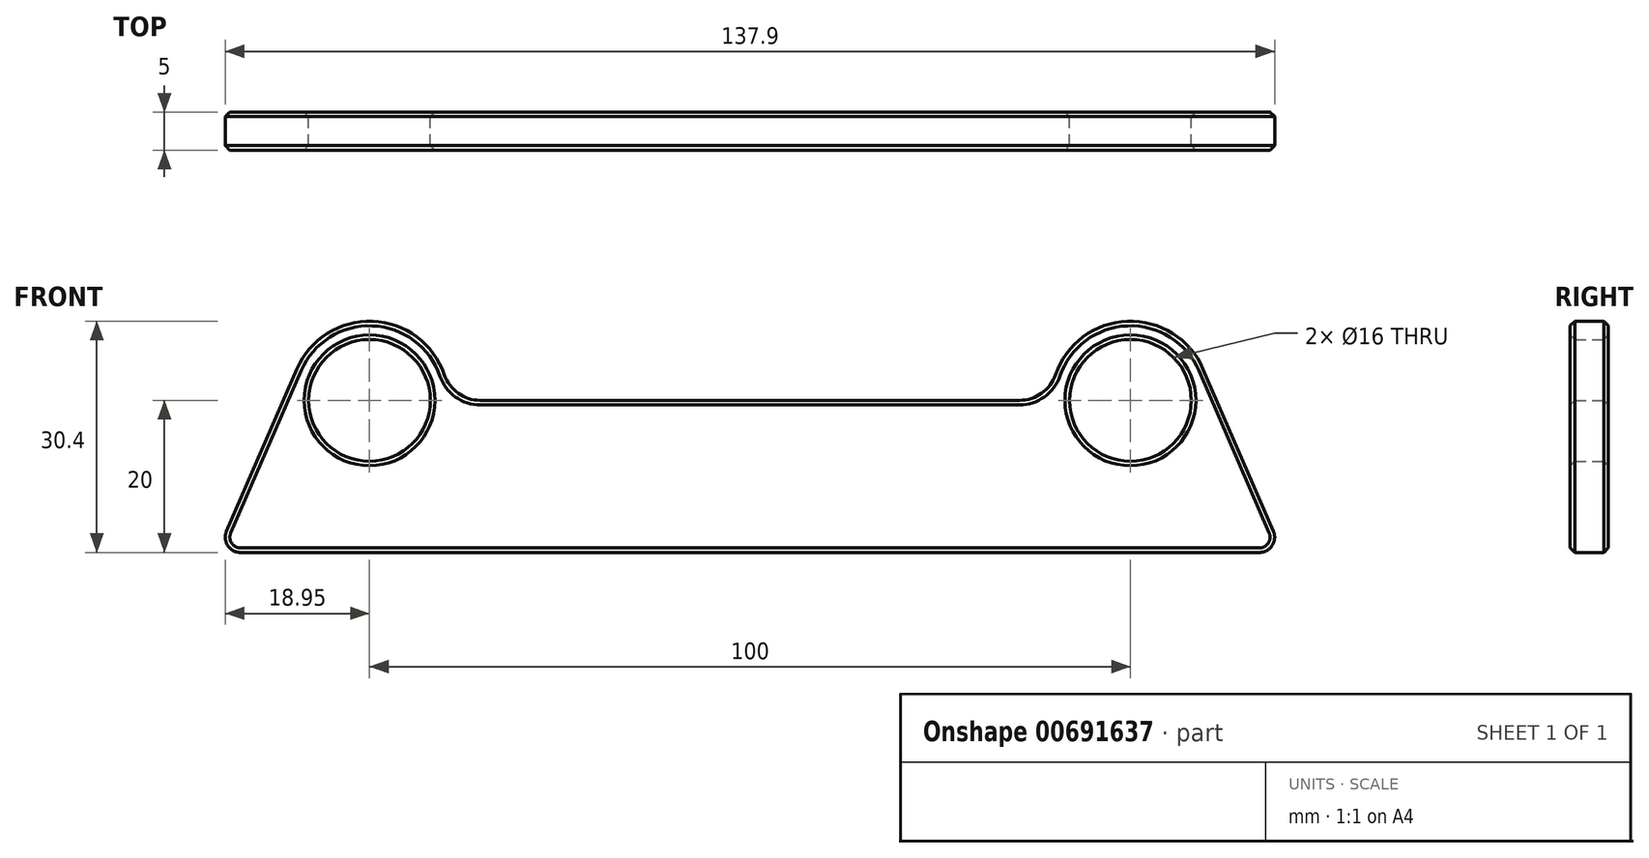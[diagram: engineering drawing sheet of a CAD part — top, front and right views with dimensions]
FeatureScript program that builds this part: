
annotation { "Feature Type Name" : "Feature", "Feature Type Description" : "" }
export const myFeature = defineFeature(function(context is Context, id is Id, definition is map)
    precondition{}
    {
        {
            var Q0;
            Q0=qCreatedBy(makeId("Front.planeOp"),FACE);
            var sketch = newSketch(context, id + "F0", { "sketchPlane" : qUnion([Q0])});
            skCircle(sketch, "E0", {"center": v(-50, 20) * mm, "radius": 2.5 * mm, "construction": true});
            skLineSegment(sketch, "E1", {"start": v(0, 0) * mm, "end": v(0, 62.59) * mm, "construction": true});
            skCircle(sketch, "E2", {"center": v(-50, 20) * mm, "radius": 8 * mm});
            skCircle(sketch, "E3.0", {"center": v(-50, 20) * mm, "radius": 10.4 * mm});
            skLineSegment(sketch, "E4", {"start": v(-70, 0) * mm, "end": v(-30, 0) * mm});
            skLineSegment(sketch, "E5", {"start": v(-50, 20) * mm, "end": v(-50, 0) * mm, "construction": true});
            skLineSegment(sketch, "E6", {"start": v(-59.54, 24.13) * mm, "end": v(-70, 0) * mm});
            skLineSegment(sketch, "E7", {"start": v(-39.6, 20) * mm, "end": v(0, 20) * mm});
            skLineSegment(sketch, "E8", {"start": v(0, 20) * mm, "end": v(0, 0) * mm});
            skLineSegment(sketch, "E9", {"start": v(-30, 0) * mm, "end": v(0, 0) * mm});
            skSolve(sketch);
        }
        {
            var Q0;
            Q0 = qSketchRegion(id + "F0", true);
            extrude(context, id + "F1", {"entities" : qUnion([Q0]), "depth" : 5 * mm, "offsetDistance" : 25 * mm});
        }
        {
            var Q0;
            Q0=makeQuery(id+"F1.opExtrude","SWEPT_EDGE",EDGE,{"disambiguationData":[OSD([sQuery(id+"F0.wireOp",EDGE,"E3.0"),sQuery(id+"F0.wireOp",EDGE,"E7")])]});
            var Q1;
            Q1=makeQuery(id+"F1.opExtrude","SWEPT_EDGE",EDGE,{"disambiguationData":[OSD([sQuery(id+"F0.wireOp",EDGE,"E3.0"),sQuery(id+"F0.wireOp",EDGE,"E6")])]});
            fillet(context, id + "F2", {"entities" : qUnion([Q0, Q1]), "radius" : 5 * mm, "tangentPropagation" : true, "allowEdgeOverflow" : false});
        }
        {
            var Q0;
            Q0=makeQuery(id+"F1.opExtrude","SWEPT_EDGE",EDGE,{"disambiguationData":[OSD([sQuery(id+"F0.wireOp",EDGE,"E4"),sQuery(id+"F0.wireOp",EDGE,"E6")])]});
            fillet(context, id + "F3", {"entities" : qUnion([Q0]), "radius" : 2 * mm, "tangentPropagation" : true, "allowEdgeOverflow" : false});
        }
        {
            var Q0;
            Q0=makeQuery(id+"F1.opExtrude","SWEPT_BODY",BODY,{"disambiguationData":[OSD([sQuery(id+"F0.wireOp",EDGE,"E2"),sQuery(id+"F0.wireOp",EDGE,"E3.0"),sQuery(id+"F0.wireOp",EDGE,"E4"),sQuery(id+"F0.wireOp",EDGE,"E6"),sQuery(id+"F0.wireOp",EDGE,"E7"),sQuery(id+"F0.wireOp",EDGE,"E8"),sQuery(id+"F0.wireOp",EDGE,"E9")])]});
            var Q1;
            Q1=makeQuery(id+"F1.opExtrude","SWEPT_FACE",FACE,{"disambiguationData":[OSD([sQuery(id+"F0.wireOp",EDGE,"E8")])]});
            mirror(context, id + "F4", {"operationType" : NewBodyOperationType.ADD, "entities" : qUnion([Q0]), "mirrorPlane" : qUnion([Q1])});
        }
        {
            var Q0;
            {var subQ0=makeQuery(id+"F1.opExtrude","CAP_FACE",FACE,{"disambiguationData":[OSD([sQuery(id+"F0.wireOp",EDGE,"E2"),sQuery(id+"F0.wireOp",EDGE,"E3.0"),sQuery(id+"F0.wireOp",EDGE,"E4"),sQuery(id+"F0.wireOp",EDGE,"E6"),sQuery(id+"F0.wireOp",EDGE,"E7"),sQuery(id+"F0.wireOp",EDGE,"E8"),sQuery(id+"F0.wireOp",EDGE,"E9")])],"isStart":false});Q0=makeQuery(id+"F4.boolean.opBoolean","MERGE",FACE,{"derivedFrom":[subQ0,makeQuery(id+"F4.opPattern","COPY",FACE,{"derivedFrom":subQ0,"instanceName":"1"})]});}
            var Q1;
            {var subQ0=makeQuery(id+"F1.opExtrude","CAP_FACE",FACE,{"disambiguationData":[OSD([sQuery(id+"F0.wireOp",EDGE,"E2"),sQuery(id+"F0.wireOp",EDGE,"E3.0"),sQuery(id+"F0.wireOp",EDGE,"E4"),sQuery(id+"F0.wireOp",EDGE,"E6"),sQuery(id+"F0.wireOp",EDGE,"E7"),sQuery(id+"F0.wireOp",EDGE,"E8"),sQuery(id+"F0.wireOp",EDGE,"E9")])],"isStart":true});Q1=makeQuery(id+"F4.boolean.opBoolean","MERGE",FACE,{"derivedFrom":[subQ0,makeQuery(id+"F4.opPattern","COPY",FACE,{"derivedFrom":subQ0,"instanceName":"1"})]});}
            chamfer(context, id + "F5", {"entities" : qUnion([Q0, Q1]), "width" : .6 * mm, "tangentPropagation" : true});
        }
    });
